AUTODESK INVENTOR PART (.ipt)
format: ipt  version: 2024 (Build 280153000, 153)  size: 244,224 bytes
history: native  units: in
note: dims shown in document units (in); Inventor stores cm internally (conversion verified against a paired STEP export)
features: sketch x2, extrude x1
ambient origin geometry x8: Origin, YZ Plane, XZ Plane, XY Plane, X Axis, Y Axis, Z Axis, Center Point
bodies: Solid1 (feature_tree)
feature tree (3):
  extrude  "Extrusion1"  Depth=0.3937in TaperAngle=0.0deg
  sketch  "Sketch2"  dims[d3=0.9449in d4=0.1181in d5=0.1575in d6=0.1575in d7=0.1575in]
  sketch  "Sketch1"  dims[d0=1.378in d1=0.3937in d2=0.0in]
